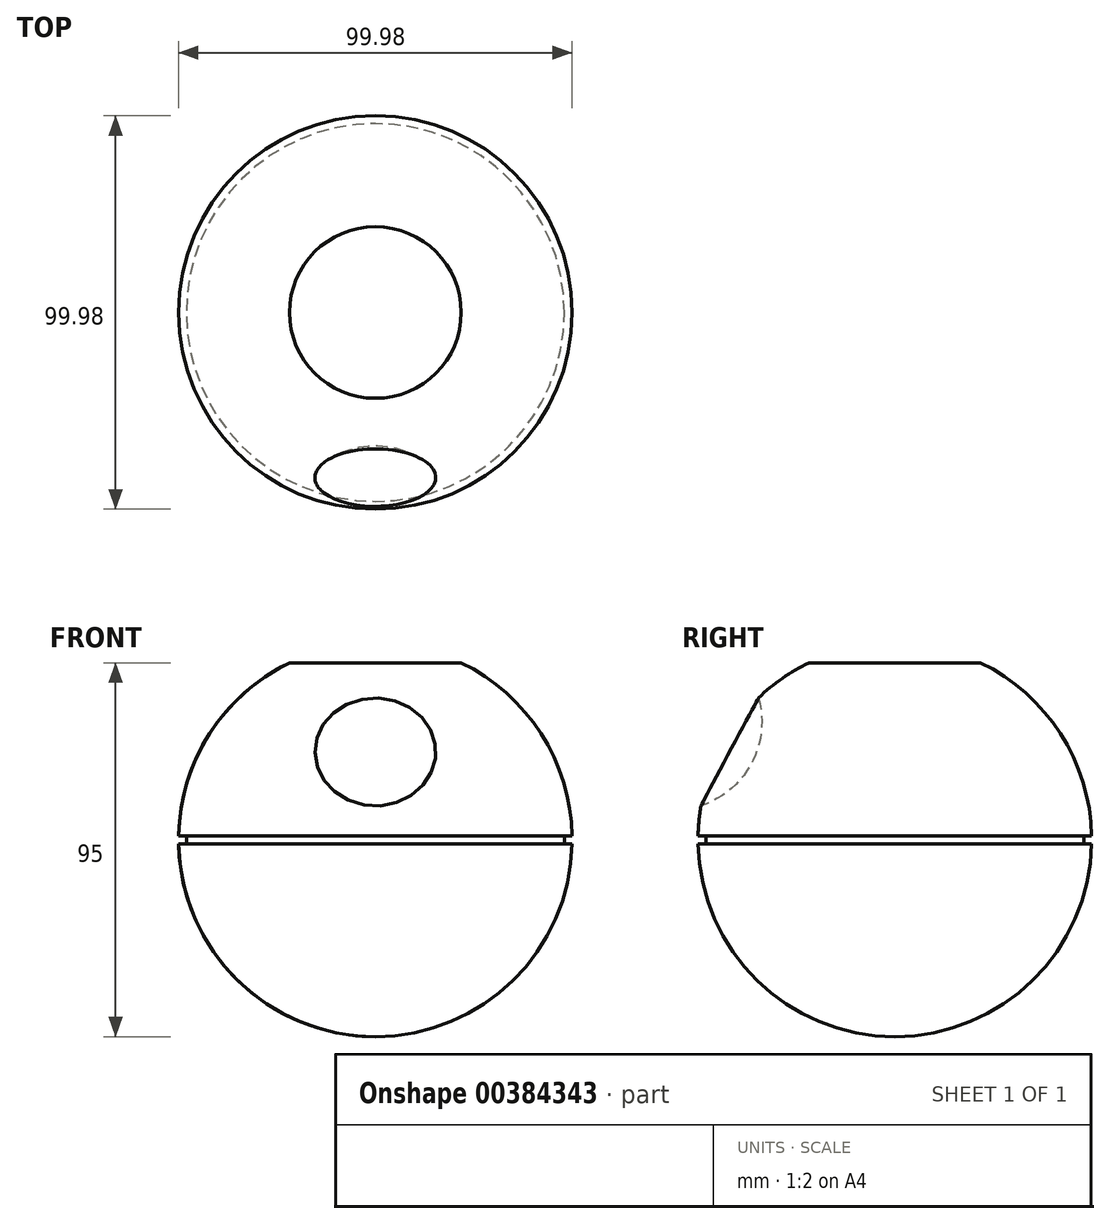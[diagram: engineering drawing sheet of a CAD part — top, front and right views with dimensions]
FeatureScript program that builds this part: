
annotation { "Feature Type Name" : "Feature", "Feature Type Description" : "" }
export const myFeature = defineFeature(function(context is Context, id is Id, definition is map)
    precondition{}
    {
        {
            var Q0;
            Q0=qCreatedBy(makeId("Front.planeOp"),FACE);
            var sketch = newSketch(context, id + "F0", { "sketchPlane" : qUnion([Q0])});
            skArc(sketch, "E0", {"start": v(0, -50) * mm, "mid": v(50, 0) * mm, "end": v(0, 50) * mm});
            skLineSegment(sketch, "E1", {"start": v(0, 50) * mm, "end": v(0, -50) * mm});
            skSolve(sketch);
        }
        {
            var Q0;
            Q0=makeQuery(id+"F0.imprint","IMPRINT",FACE,{"disambiguationData":[TD([[makeQuery(id+"F0.imprint","IMPRINT",EDGE,{"derivedFrom":sQuery(id+"F0.wireOp",EDGE,"E0")}),1.0]])]});
            var Q1;
            Q1=sQuery(id+"F0.wireOp",EDGE,"E1");
            revolve(context, id + "F1", {"entities" : qUnion([Q0]), "axis" : qUnion([Q1]), "revolveType" : RevolveType.FULL});
        }
        {
            var Q0;
            Q0=qCreatedBy(makeId("Right.planeOp"),FACE);
            var sketch = newSketch(context, id + "F2", { "sketchPlane" : qUnion([Q0])});
            skArc(sketch, "E2", {"start": v(-56.53, 7.5) * mm, "mid": v(-33.82, 29.24) * mm, "end": v(-55, 52.46) * mm});
            skLineSegment(sketch, "E3", {"start": v(-55, 52.46) * mm, "end": v(-56.53, 7.5) * mm});
            skSolve(sketch);
        }
        {
            var Q0;
            Q0=makeQuery(id+"F2.imprint","IMPRINT",FACE,{"disambiguationData":[TD([[makeQuery(id+"F2.imprint","IMPRINT",EDGE,{"derivedFrom":sQuery(id+"F2.wireOp",EDGE,"E2")}),1.0]])]});
            var Q1;
            Q1=sQuery(id+"F2.wireOp",EDGE,"E3");
            revolve(context, id + "F3", {"operationType" : NewBodyOperationType.REMOVE, "entities" : qUnion([Q0]), "axis" : qUnion([Q1]), "revolveType" : RevolveType.FULL, "oppositeDirection" : true});
        }
        {
            var Q0;
            Q0=qCreatedBy(makeId("Front.planeOp"),FACE);
            var sketch = newSketch(context, id + "F4", { "sketchPlane" : qUnion([Q0])});
            skLineSegment(sketch, "E4.bottom", {"start": v(-63.8, 61.9) * mm, "end": v(62.76, 61.9) * mm});
            skLineSegment(sketch, "E4.top", {"start": v(-63.8, 45) * mm, "end": v(62.76, 45) * mm});
            skLineSegment(sketch, "E4.left", {"start": v(-63.8, 61.9) * mm, "end": v(-63.8, 45) * mm});
            skLineSegment(sketch, "E4.right", {"start": v(62.76, 61.9) * mm, "end": v(62.76, 45) * mm});
            skSolve(sketch);
        }
        {
            var Q0;
            Q0 = qSketchRegion(id + "F4", true);
            extrude(context, id + "F5", {"entities" : qUnion([Q0]), "operationType" : NewBodyOperationType.REMOVE, "oppositeDirection" : true, "depth" : 25 * mm, "hasSecondDirection" : true, "secondDirectionOppositeDirection" : false, "secondDirectionDepth" : 25 * mm});
        }
        {
            var Q0;
            Q0=qCreatedBy(makeId("Front.planeOp"),FACE);
            var sketch = newSketch(context, id + "F6", { "sketchPlane" : qUnion([Q0])});
            skLineSegment(sketch, "E5", {"start": v(0, 53.94) * mm, "end": v(0, -53.94) * mm, "construction": true});
            skLineSegment(sketch, "E6.bottom", {"start": v(-70.83, 1) * mm, "end": v(-48, 1) * mm});
            skLineSegment(sketch, "E6.top", {"start": v(-70.83, -1) * mm, "end": v(-48, -1) * mm});
            skLineSegment(sketch, "E6.left", {"start": v(-70.83, 1) * mm, "end": v(-70.83, -1) * mm});
            skLineSegment(sketch, "E6.right", {"start": v(-48, 1) * mm, "end": v(-48, -1) * mm});
            skSolve(sketch);
        }
        {
            var Q0;
            Q0 = qSketchRegion(id + "F6", true);
            var Q1;
            Q1=sQuery(id+"F6.wireOp",EDGE,"E5");
            revolve(context, id + "F7", {"operationType" : NewBodyOperationType.REMOVE, "entities" : qUnion([Q0]), "axis" : qUnion([Q1]), "revolveType" : RevolveType.FULL, "oppositeDirection" : true});
        }
    });
